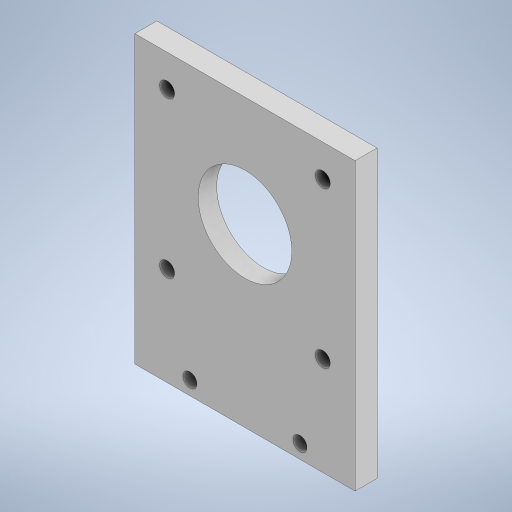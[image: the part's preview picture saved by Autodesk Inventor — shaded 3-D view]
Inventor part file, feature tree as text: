
AUTODESK INVENTOR PART (.ipt)
format: ipt  version: 2024 (Build 280153000, 153)  size: 270,336 bytes
history: native  units: in
note: dims shown in document units (in); Inventor stores cm internally (conversion verified against a paired STEP export)
features: extrude x4, sketch x4
ambient origin geometry x8: Origin, YZ Plane, XZ Plane, XY Plane, X Axis, Y Axis, Z Axis, Center Point
bodies: Solid1 (feature_tree)
feature tree (8):
  extrude  "Extrusion1"  Depth=10.2362in
  extrude  "Extrusion2"  Depth=0.7874in
  extrude  "Extrusion6"  Depth=3.937in
  extrude  "Extrusion10"  Depth=0.126in
  sketch  "Sketch1"  dims[d0=7.874in d1=10.2362in]
  sketch  "Sketch2"  dims[d2=0.7874in d3=0.0in d4=3.3465in]
  sketch  "Sketch6"  dims[d5=3.937in d6=3.937in]
  sketch  "Sketch11"  dims[d7=1.1811in d8=0.0in d18=2.7839in d19=2.7839in d20=2.7839in d21=2.7839in d22=2.7839in d23=2.7839in d24=2.7839in d25=2.7839in d26=0.5315in d27=0.5315in d28=0.5315in d29=0.5315in d30=0.7874in d31=0.0in d57=0.5in d58=0.5in d59=1.969in d60=1.969in d61=0.492in d62=0.492in d63=4.5in d64=0.126in d65=0.0in]
